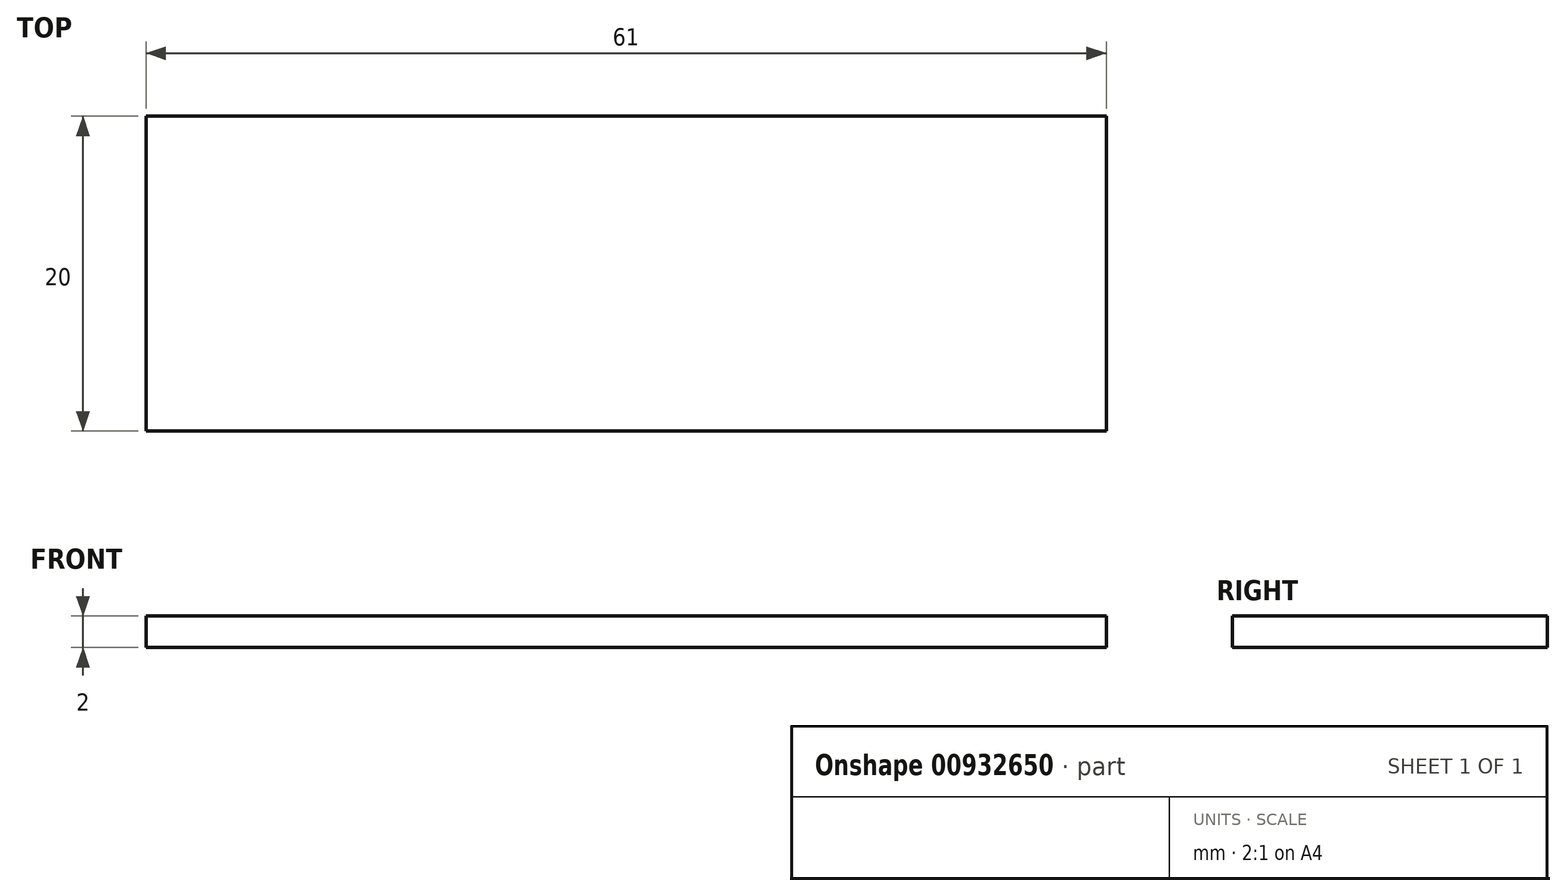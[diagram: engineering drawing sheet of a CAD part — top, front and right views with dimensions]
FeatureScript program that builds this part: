
annotation { "Feature Type Name" : "Feature", "Feature Type Description" : "" }
export const myFeature = defineFeature(function(context is Context, id is Id, definition is map)
    precondition{}
    {
        {
            var Q0;
            Q0=qCreatedBy(makeId("Top.planeOp"), FACE);
            var sketch = newSketch(context, id + "F0", { "sketchPlane" : qUnion([Q0])});
            skLineSegment(sketch, "E0.bottom", {"start": v(30.5, -10) * mm, "end": v(-30.5, -10) * mm});
            skLineSegment(sketch, "E0.top", {"start": v(30.5, 10) * mm, "end": v(-30.5, 10) * mm});
            skLineSegment(sketch, "E0.left", {"start": v(30.5, -10) * mm, "end": v(30.5, 10) * mm});
            skLineSegment(sketch, "E0.right", {"start": v(-30.5, -10) * mm, "end": v(-30.5, 10) * mm});
            skPoint(sketch, "E0.middle", {"position": v(0, 0) * mm});
            skSolve(sketch);
        }
        {
            var Q0;
            Q0 = qSketchRegion(id + "F0", true);
            extrude(context, id + "F1", {"entities" : qUnion([Q0]), "depth" : 2 * mm, "offsetDistance" : 25 * mm});
        }
    });
